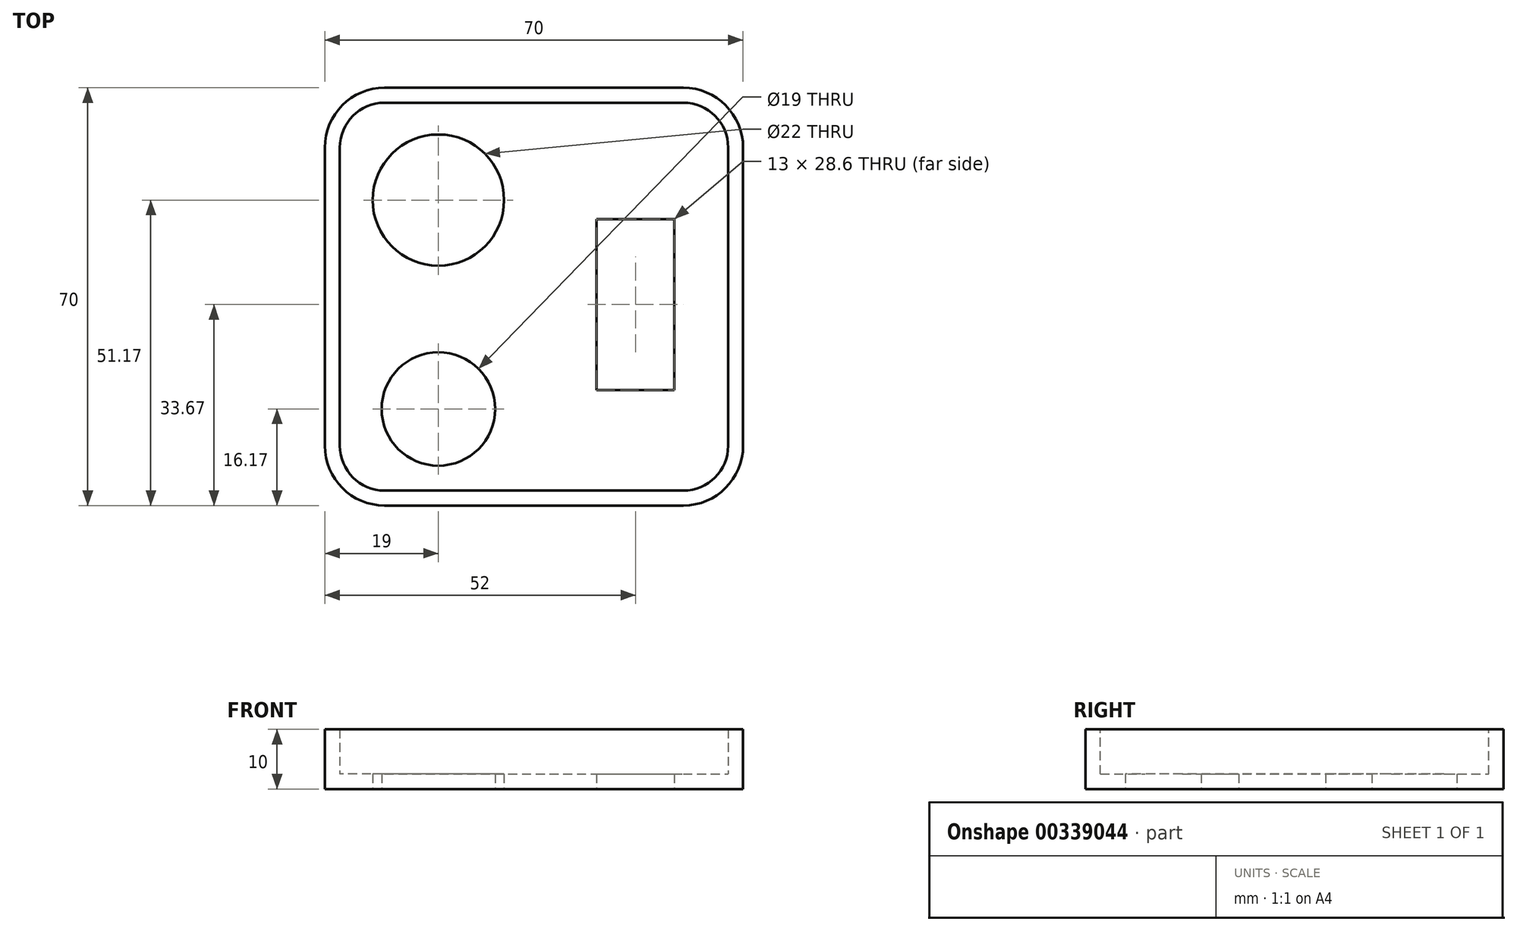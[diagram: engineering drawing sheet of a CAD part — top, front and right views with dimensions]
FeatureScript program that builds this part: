
annotation { "Feature Type Name" : "Feature", "Feature Type Description" : "" }
export const myFeature = defineFeature(function(context is Context, id is Id, definition is map)
    precondition{}
    {
        {
            var Q0;
            Q0=qCreatedBy(makeId("Top.planeOp"),FACE);
            var sketch = newSketch(context, id + "F0", { "sketchPlane" : qUnion([Q0])});
            skLineSegment(sketch, "E0.bottom", {"start": v(-35, 36.33) * mm, "end": v(35, 36.33) * mm});
            skLineSegment(sketch, "E0.top", {"start": v(-35, -33.67) * mm, "end": v(35, -33.67) * mm});
            skLineSegment(sketch, "E0.left", {"start": v(-35, 36.33) * mm, "end": v(-35, -33.67) * mm});
            skLineSegment(sketch, "E0.right", {"start": v(35, 36.33) * mm, "end": v(35, -33.67) * mm});
            skPoint(sketch, "E0.middle", {"position": v(0, 1.33) * mm});
            skSolve(sketch);
        }
        {
            var Q0;
            Q0 = qSketchRegion(id + "F0", true);
            extrude(context, id + "F1", {"entities" : qUnion([Q0]), "depth" : 10 * mm});
        }
        {
            var Q0;
            Q0=makeQuery(id+"F1.opExtrude","SWEPT_EDGE",EDGE,{"disambiguationData":[OSD([sQuery(id+"F0.wireOp",EDGE,"E0.bottom"),sQuery(id+"F0.wireOp",EDGE,"E0.right")])]});
            var Q1;
            Q1=makeQuery(id+"F1.opExtrude","SWEPT_EDGE",EDGE,{"disambiguationData":[OSD([sQuery(id+"F0.wireOp",EDGE,"E0.top"),sQuery(id+"F0.wireOp",EDGE,"E0.right")])]});
            var Q2;
            Q2=makeQuery(id+"F1.opExtrude","SWEPT_EDGE",EDGE,{"disambiguationData":[OSD([sQuery(id+"F0.wireOp",EDGE,"E0.bottom"),sQuery(id+"F0.wireOp",EDGE,"E0.left")])]});
            var Q3;
            Q3=makeQuery(id+"F1.opExtrude","SWEPT_EDGE",EDGE,{"disambiguationData":[OSD([sQuery(id+"F0.wireOp",EDGE,"E0.top"),sQuery(id+"F0.wireOp",EDGE,"E0.left")])]});
            fillet(context, id + "F2", {"entities" : qUnion([Q0, Q1, Q2, Q3]), "radius" : 10 * mm, "tangentPropagation" : true, "allowEdgeOverflow" : false});
        }
        {
            var Q0;
            Q0=makeQuery(id+"F1.opExtrude","CAP_FACE",FACE,{"disambiguationData":[OSD([sQuery(id+"F0.wireOp",EDGE,"E0.bottom"),sQuery(id+"F0.wireOp",EDGE,"E0.top"),sQuery(id+"F0.wireOp",EDGE,"E0.left"),sQuery(id+"F0.wireOp",EDGE,"E0.right")])],"isStart":false});
            shell(context, id + "F3", {"entities" : qUnion([Q0]), "thickness" : 2.5 * mm});
        }
        {
            var Q0;
            Q0=makeQuery(id+"F1.opExtrude","CAP_FACE",FACE,{"disambiguationData":[OSD([sQuery(id+"F0.wireOp",EDGE,"E0.bottom"),sQuery(id+"F0.wireOp",EDGE,"E0.top"),sQuery(id+"F0.wireOp",EDGE,"E0.left"),sQuery(id+"F0.wireOp",EDGE,"E0.right")])],"isStart":true});
            var sketch = newSketch(context, id + "F4", { "sketchPlane" : qUnion([Q0])});
            skLineSegment(sketch, "E1.bottom", {"start": v(23.5, -14.3) * mm, "end": v(10.5, -14.3) * mm});
            skLineSegment(sketch, "E1.top", {"start": v(23.5, 14.3) * mm, "end": v(10.5, 14.3) * mm});
            skLineSegment(sketch, "E1.left", {"start": v(23.5, -14.3) * mm, "end": v(23.5, 14.3) * mm});
            skLineSegment(sketch, "E1.right", {"start": v(10.5, -14.3) * mm, "end": v(10.5, 14.3) * mm});
            skPoint(sketch, "E1.middle", {"position": v(17, 0) * mm});
            skLineSegment(sketch, "E2", {"start": v(0, 0) * mm, "end": v(17, 0) * mm, "construction": true});
            skLineSegment(sketch, "E3", {"start": v(0, 0) * mm, "end": v(0, -17.5) * mm, "construction": true});
            skLineSegment(sketch, "E4", {"start": v(0, -17.5) * mm, "end": v(-16, -17.5) * mm, "construction": true});
            skCircle(sketch, "E5", {"center": v(-16, -17.5) * mm, "radius": 11 * mm});
            skLineSegment(sketch, "E6", {"start": v(0, 0) * mm, "end": v(0, 17.5) * mm, "construction": true});
            skLineSegment(sketch, "E7", {"start": v(0, 17.5) * mm, "end": v(-16, 17.5) * mm, "construction": true});
            skCircle(sketch, "E8", {"center": v(-16, 17.5) * mm, "radius": 9.5 * mm});
            skSolve(sketch);
        }
        {
            var Q0;
            Q0 = qSketchRegion(id + "F4", true);
            extrude(context, id + "F5", {"entities" : qUnion([Q0]), "operationType" : NewBodyOperationType.REMOVE, "oppositeDirection" : true, "depth" : 25 * mm});
        }
    });
